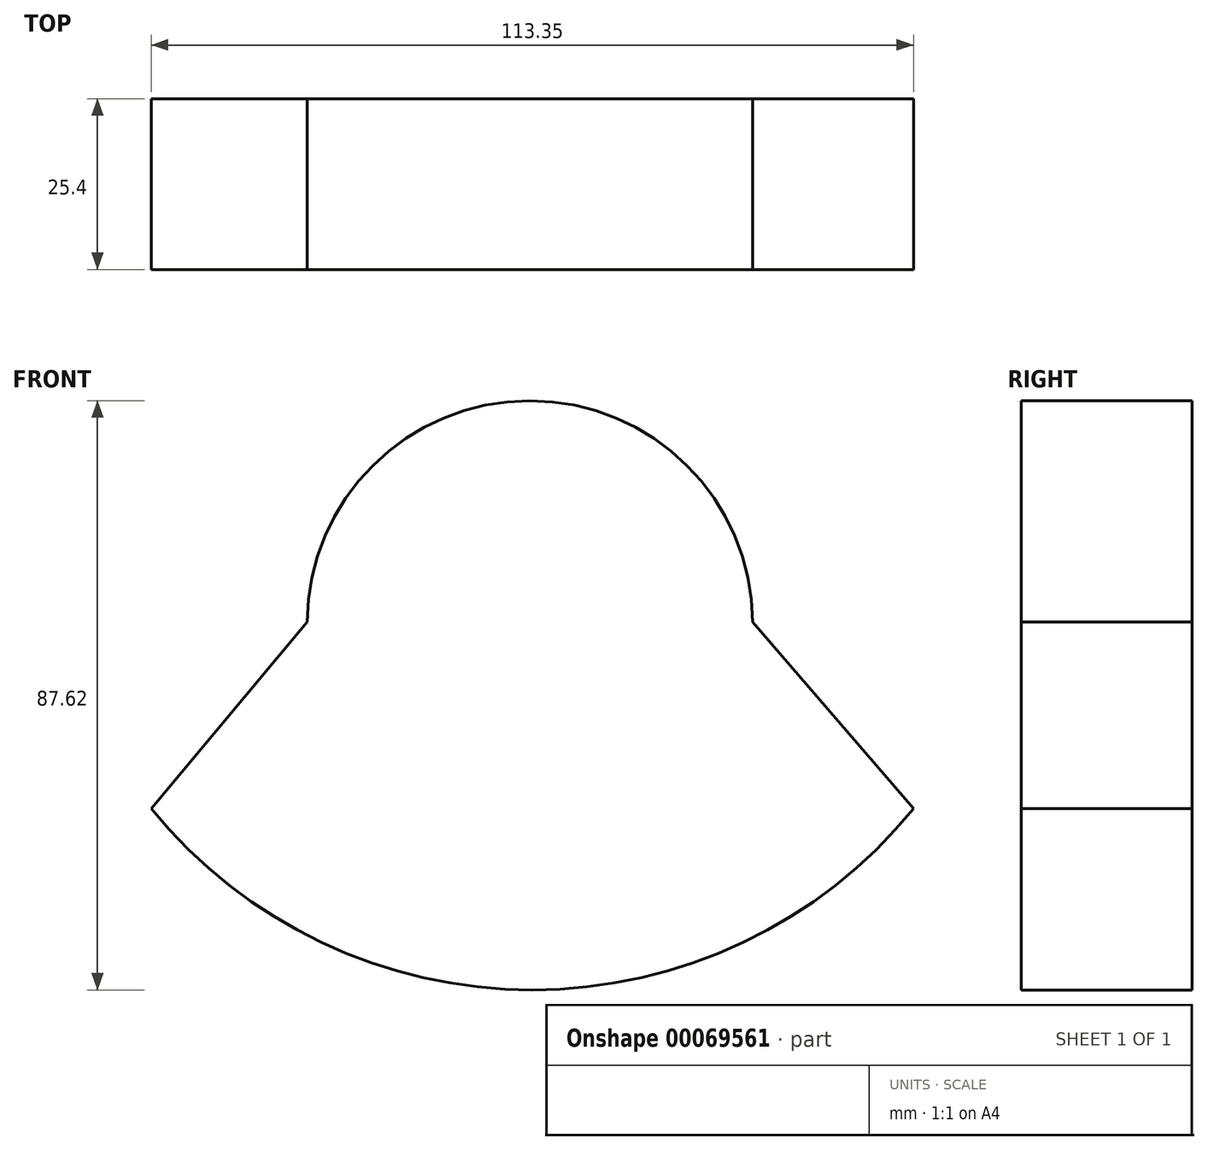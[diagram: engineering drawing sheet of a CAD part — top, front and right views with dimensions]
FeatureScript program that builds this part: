
annotation { "Feature Type Name" : "Feature", "Feature Type Description" : "" }
export const myFeature = defineFeature(function(context is Context, id is Id, definition is map)
    precondition{}
    {
        {
            var Q0;
            Q0=qCreatedBy(makeId("Front.planeOp"),FACE);
            var sketch = newSketch(context, id + "F0", { "sketchPlane" : qUnion([Q0])});
            skCircle(sketch, "E0", {"center": v(0, 0) * mm, "radius": 33.02 * mm});
            skSolve(sketch);
        }
        {
            var Q0;
            Q0=sQuery(id+"F0.wireOp",EDGE,"E0");
            extrude(context, id + "F1", {"bodyType" : ToolBodyType.SURFACE, "operationType" : NewBodyOperationType.ADD, "surfaceEntities" : qUnion([Q0]), "depth" : 111.76 * mm});
        }
        {
            var Q0;
            Q0=qCreatedBy(makeId("Front.planeOp"),FACE);
            var sketch = newSketch(context, id + "F2", { "sketchPlane" : qUnion([Q0])});
            skArc(sketch, "E1", {"start": v(33, 0) * mm, "mid": v(-0.12, 32.93) * mm, "end": v(-33.25, 0) * mm});
            skLineSegment(sketch, "E2", {"start": v(-33.25, 0) * mm, "end": v(-56.42, -27.74) * mm});
            skLineSegment(sketch, "E3", {"start": v(33, 0) * mm, "end": v(56.93, -27.74) * mm});
            skArc(sketch, "E4", {"start": v(-56.42, -27.74) * mm, "mid": v(0.25, -54.69) * mm, "end": v(56.93, -27.74) * mm});
            skLineSegment(sketch, "E5", {"start": v(-33.25, 0) * mm, "end": v(-56.42, 28.37) * mm});
            skLineSegment(sketch, "E6", {"start": v(33, 0) * mm, "end": v(56.93, 27.74) * mm});
            skArc(sketch, "E7", {"start": v(56.93, 27.74) * mm, "mid": v(0.4, 55.1) * mm, "end": v(-56.42, 28.37) * mm});
            skSolve(sketch);
        }
        {
            var Q0;
            Q0=makeQuery(id+"F2.imprint","IMPRINT",FACE,{"disambiguationData":[TD([[makeQuery(id+"F2.imprint","IMPRINT",EDGE,{"derivedFrom":sQuery(id+"F2.wireOp",EDGE,"E1")}),1.0]])]});
            extrude(context, id + "F3", {"entities" : qUnion([Q0]), "depth" : 25.4 * mm});
        }
    });
